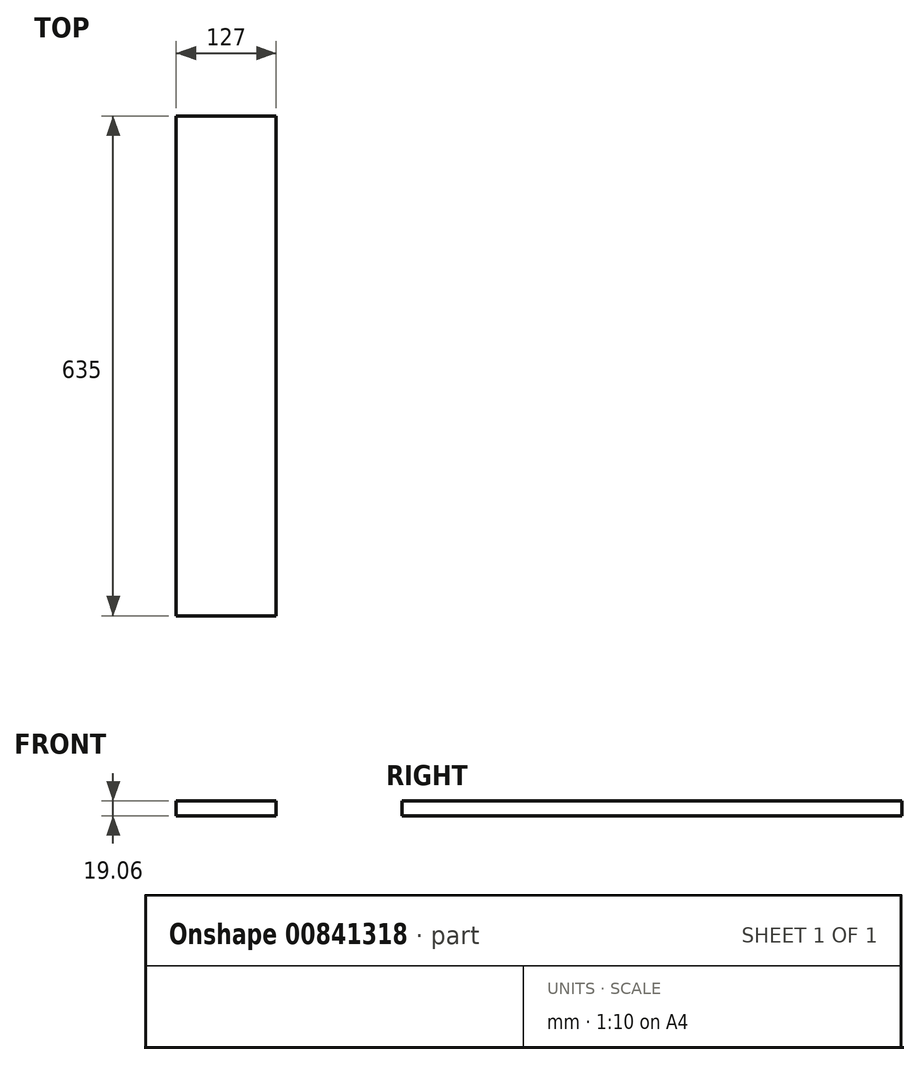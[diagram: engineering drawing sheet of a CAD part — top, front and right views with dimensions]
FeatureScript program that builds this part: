
annotation { "Feature Type Name" : "Feature", "Feature Type Description" : "" }
export const myFeature = defineFeature(function(context is Context, id is Id, definition is map)
    precondition{}
    {
        {
            var Q0;
            Q0=qCreatedBy(makeId("Front.planeOp"),FACE);
            var sketch = newSketch(context, id + "F0", { "sketchPlane" : qUnion([Q0])});
            skLineSegment(sketch, "E0.bottom", {"start": v(-63.5, 9.52) * mm, "end": v(63.5, 9.53) * mm});
            skLineSegment(sketch, "E0.top", {"start": v(-63.5, -9.53) * mm, "end": v(63.5, -9.52) * mm});
            skLineSegment(sketch, "E0.left", {"start": v(-63.5, 9.52) * mm, "end": v(-63.5, -9.53) * mm});
            skLineSegment(sketch, "E0.right", {"start": v(63.5, 9.53) * mm, "end": v(63.5, -9.52) * mm});
            skSolve(sketch);
        }
        {
            var Q0;
            Q0 = qSketchRegion(id + "F0", true);
            extrude(context, id + "F1", {"entities" : qUnion([Q0]), "depth" : 317.5 * mm, "offsetDistance" : 25.4 * mm, "hasSecondDirection" : true, "secondDirectionOppositeDirection" : true, "secondDirectionDepth" : 317.5 * mm});
        }
    });
